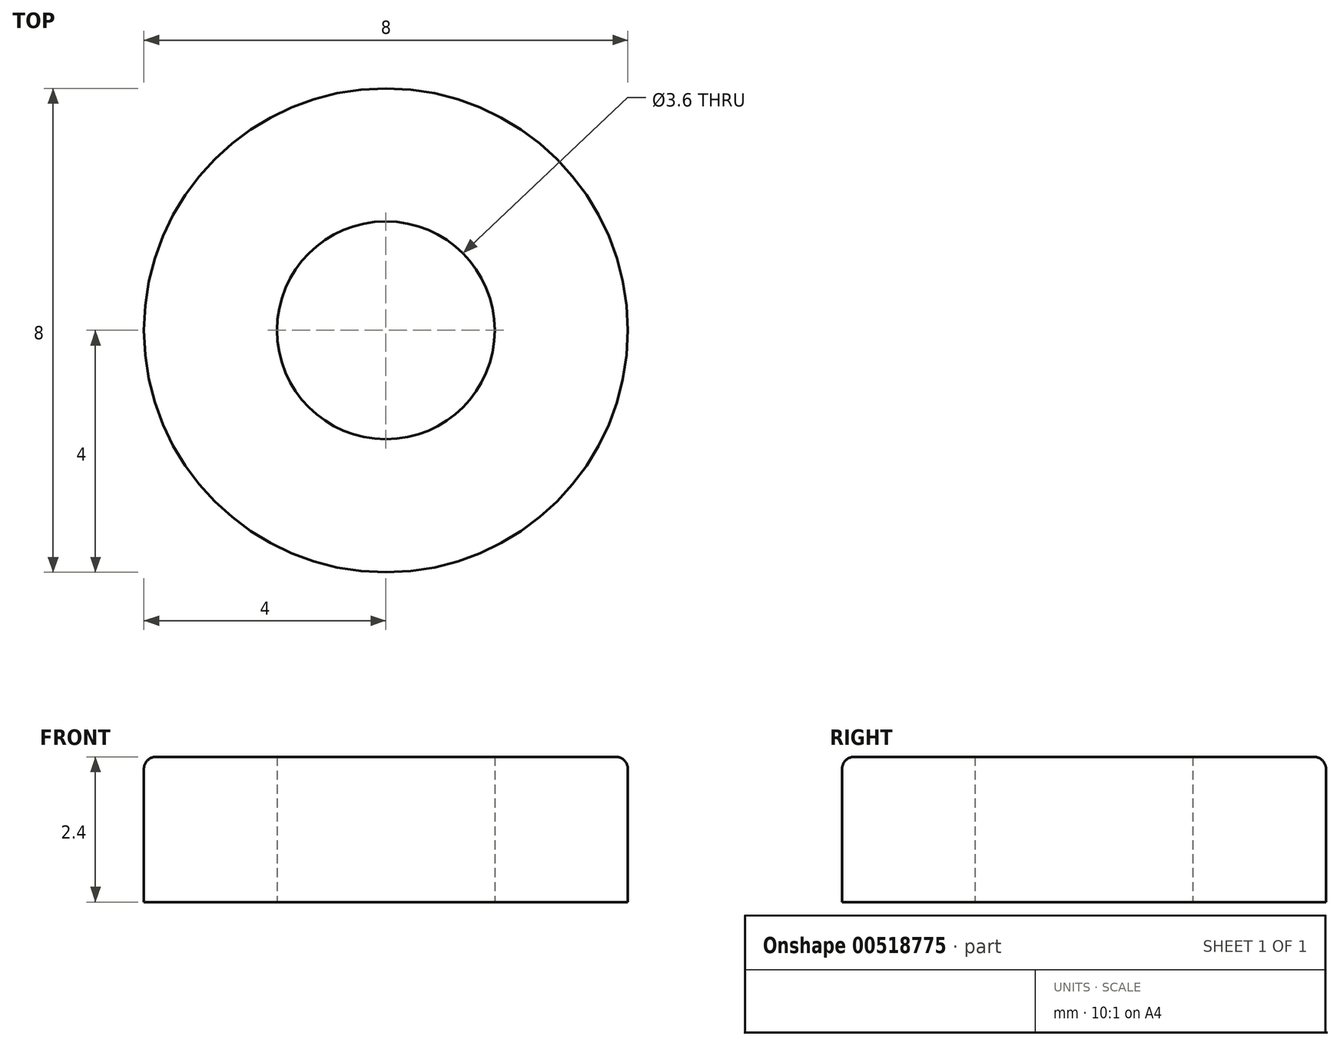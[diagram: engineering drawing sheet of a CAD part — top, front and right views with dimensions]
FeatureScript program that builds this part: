
annotation { "Feature Type Name" : "Feature", "Feature Type Description" : "" }
export const myFeature = defineFeature(function(context is Context, id is Id, definition is map)
    precondition{}
    {
        {
            var Q0;
            Q0=qCreatedBy(makeId("Top.planeOp"),FACE);
            var sketch = newSketch(context, id + "F0", { "sketchPlane" : qUnion([Q0])});
            skCircle(sketch, "E0", {"center": v(0, 0) * mm, "radius": 4 * mm});
            skCircle(sketch, "E1", {"center": v(0, 0) * mm, "radius": 4.1 * mm});
            skSolve(sketch);
        }
        {
            var Q0;
            Q0=makeQuery(id+"F0.imprint","IMPRINT",FACE,{"disambiguationData":[TD([[makeQuery(id+"F0.imprint","IMPRINT",EDGE,{"derivedFrom":sQuery(id+"F0.wireOp",EDGE,"E0")}),1.0]])]});
            extrude(context, id + "F1", {"entities" : qUnion([Q0]), "depth" : 2.4 * mm, "offsetDistance" : 25 * mm});
        }
        {
            var Q0;
            Q0=sQuery(id+"F0.wireOp",VERTEX,"E0.center");
            var Q1;
            Q1=makeQuery(id+"F1.opExtrude","SWEPT_BODY",BODY,{"disambiguationData":[OSD([sQuery(id+"F0.wireOp",EDGE,"E0")])]});
            hole(context, id + "F2", {"style" : HoleStyle.SIMPLE, "endStyle" : HoleEndStyle.THROUGH, "oppositeDirection" : true, "holeDiameter" : 3.6 * mm, "isTappedThrough" : true, "tappedDepth" : 12 * mm, "tapClearance" : 3, "locations" : qUnion([Q0]), "scope" : qUnion([Q1])});
        }
        {
            var Q0;
            Q0=makeQuery(id+"F1.opExtrude","CAP_EDGE",EDGE,{"disambiguationData":[OSD([sQuery(id+"F0.wireOp",EDGE,"E0")])],"isStart":false});
            var Q1;
            Q1=makeQuery(id+"F2.hole-0.boolean.opBoolean","INTERSECT",EDGE,{"derivedFrom":[makeQuery(id+"F1.opExtrude","CAP_FACE",FACE,{"disambiguationData":[OSD([sQuery(id+"F0.wireOp",EDGE,"E0")])],"isStart":false}),makeQuery(id+"F2.hole-0.opRevolve","SWEPT_FACE",FACE,{"disambiguationData":[OSD([sQuery(id+"F2.hole-0.sketch.wireOp",EDGE,"core_line_2")])]})]});
            fillet(context, id + "F3", {"entities" : qUnion([Q0, Q1]), "radius" : 0.2 * mm, "tangentPropagation" : true, "allowEdgeOverflow" : false});
        }
    });
